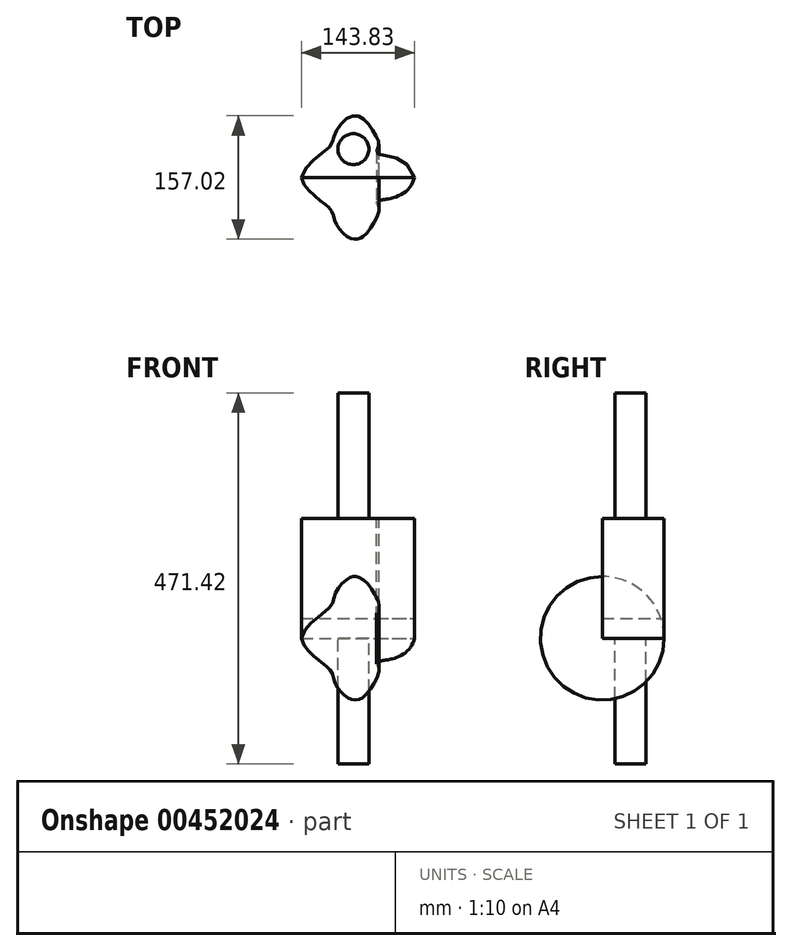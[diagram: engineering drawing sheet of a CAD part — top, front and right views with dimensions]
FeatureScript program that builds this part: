
annotation { "Feature Type Name" : "Feature", "Feature Type Description" : "" }
export const myFeature = defineFeature(function(context is Context, id is Id, definition is map)
    precondition{}
    {
        {
            var Q0;
            Q0=qCreatedBy(makeId("Top.planeOp"),FACE);
            var sketch = newSketch(context, id + "F0", { "sketchPlane" : qUnion([Q0])});
            skFitSpline(sketch, "E0", {"points": [v(0, 0) * mm, v(36.74, 40.2) * mm, v(42.83, 56.2) * mm, v(61.97, 77.14) * mm, v(78.7, 74.64) * mm, v(94.03, 54.37) * mm, v(98.13, 40.01) * mm, v(96.42, 30.61) * mm, v(143.83, 0) * mm], "startDerivative": vector(58.4, 296.87) * mm, "endDerivative": vector(141.29, -503.12) * mm});
            skLineSegment(sketch, "E1", {"start": v(0, 0) * mm, "end": v(143.83, 0) * mm});
            skSolve(sketch);
        }
        {
            var Q0;
            Q0 = qSketchRegion(id + "F0", true);
            var Q1;
            Q1=sQuery(id+"F0.wireOp",EDGE,"E1");
            revolve(context, id + "F1", {"entities" : qUnion([Q0]), "axis" : qUnion([Q1]), "revolveType" : RevolveType.FULL});
        }
        {
            var Q0;
            Q0=makeQuery(id+"F0.imprint","IMPRINT",FACE,{"disambiguationData":[TD([[makeQuery(id+"F0.imprint","IMPRINT",EDGE,{"derivedFrom":sQuery(id+"F0.wireOp",EDGE,"E0")}),-1.0]])]});
            extrude(context, id + "F2", {"entities" : qUnion([Q0]), "depth" : 25.4 * mm, "offsetDistance" : 25.4 * mm});
        }
        {
            var Q0;
            Q0=makeQuery(id+"F2.opExtrude","CAP_FACE",FACE,{"disambiguationData":[OSD([sQuery(id+"F0.wireOp",EDGE,"E0"),sQuery(id+"F0.wireOp",EDGE,"E1")])],"isStart":false});
            extrude(context, id + "F3", {"entities" : qUnion([Q0]), "depth" : 127 * mm, "offsetDistance" : 25.4 * mm});
        }
        {
            var Q0;
            Q0=makeQuery(id+"F3.opExtrude","CAP_FACE",FACE,{"disambiguationData":[OSD([sQuery(id+"F0.wireOp",EDGE,"E0"),sQuery(id+"F0.wireOp",EDGE,"E1")])],"isStart":false});
            var sketch = newSketch(context, id + "F4", { "sketchPlane" : qUnion([Q0])});
            skCircle(sketch, "E2", {"center": v(66.14, 35.92) * mm, "radius": 19.62 * mm});
            skSolve(sketch);
        }
        {
            var Q0;
            Q0 = qSketchRegion(id + "F4", true);
            extrude(context, id + "F5", {"entities" : qUnion([Q0]), "depth" : 159.5 * mm, "offsetDistance" : 25.4 * mm});
        }
        {
            var Q0;
            Q0=qCreatedBy(makeId("Top.planeOp"),FACE);
            var sketch = newSketch(context, id + "F6", { "sketchPlane" : qUnion([Q0])});
            skPoint(sketch, "E3.0", {"position": v(66.14, 35.92) * mm});
            skCircle(sketch, "E4.0", {"center": v(66.14, 35.92) * mm, "radius": 19.62 * mm});
            skSolve(sketch);
        }
        {
            var Q0;
            Q0 = qSketchRegion(id + "F6", true);
            extrude(context, id + "F7", {"entities" : qUnion([Q0]), "oppositeDirection" : true, "depth" : 159.5 * mm, "offsetDistance" : 25.4 * mm});
        }
    });
